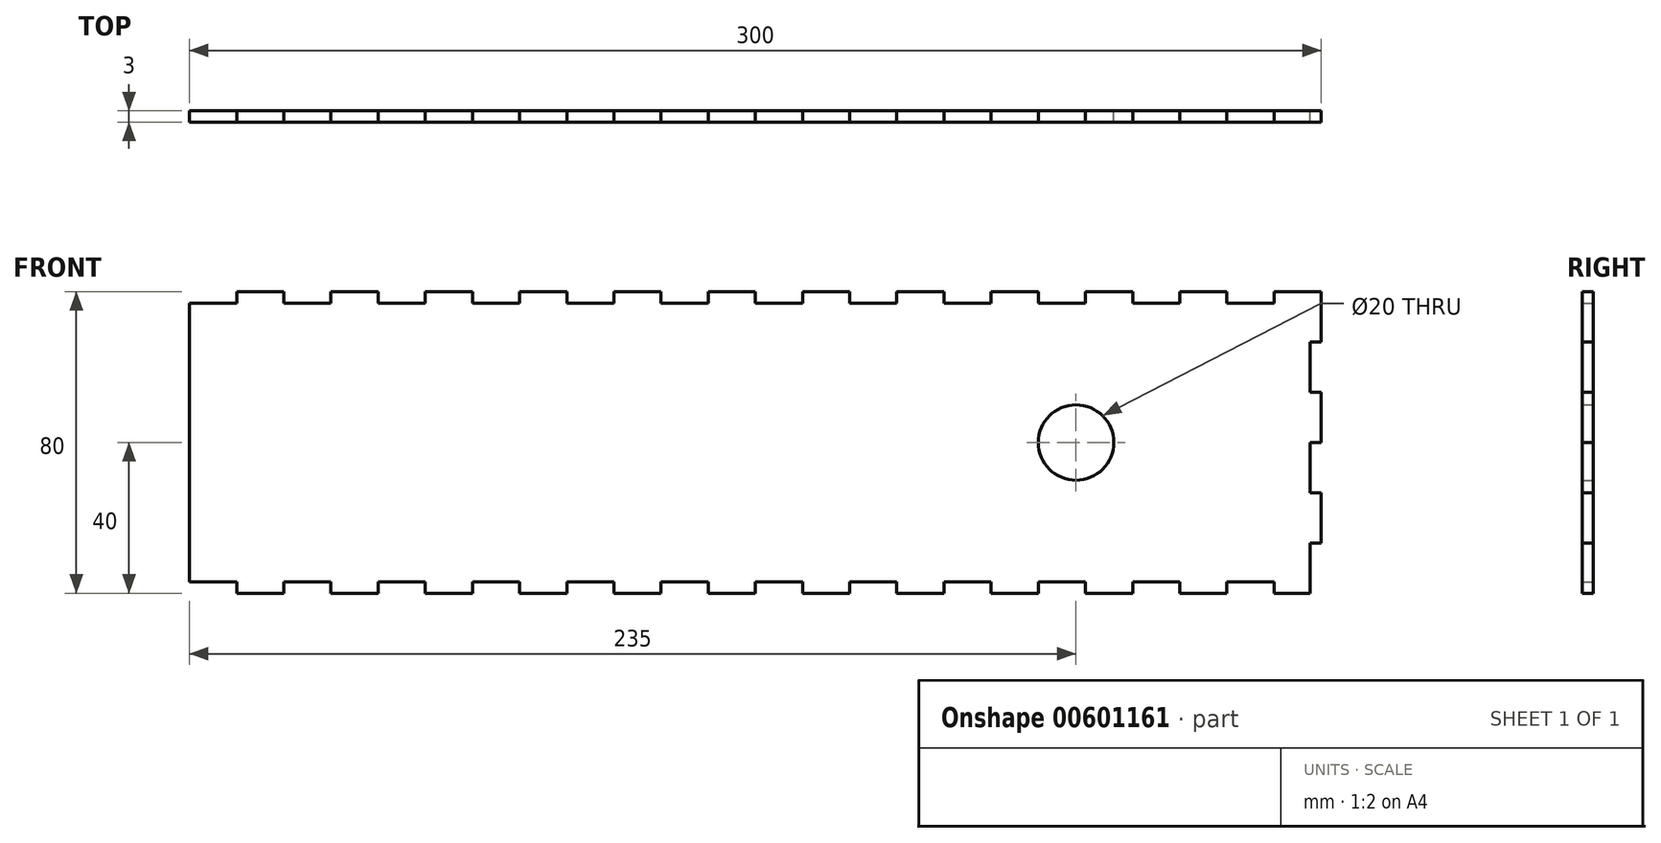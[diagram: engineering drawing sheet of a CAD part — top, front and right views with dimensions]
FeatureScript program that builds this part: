
annotation { "Feature Type Name" : "Feature", "Feature Type Description" : "" }
export const myFeature = defineFeature(function(context is Context, id is Id, definition is map)
    precondition{}
    {
        {
            var Q0;
            Q0=qCreatedBy(makeId("Front.planeOp"),FACE);
            var sketch = newSketch(context, id + "F0", { "sketchPlane" : qUnion([Q0])});
            skLineSegment(sketch, "E0.left", {"start": v(150, -26.67) * mm, "end": v(150, -13.33) * mm});
            skLineSegment(sketch, "E0.right", {"start": v(-150, -37) * mm, "end": v(-150, 37) * mm});
            skPoint(sketch, "E0.middle", {"position": v(0, 0) * mm});
            skLineSegment(sketch, "E1", {"start": v(-137.5, -40) * mm, "end": v(-125, -40) * mm});
            skLineSegment(sketch, "E2", {"start": v(-150, -37) * mm, "end": v(-137.5, -37) * mm});
            skLineSegment(sketch, "E3", {"start": v(-137.5, -37) * mm, "end": v(-137.5, -40) * mm});
            skLineSegment(sketch, "E4", {"start": v(-125, -37) * mm, "end": v(-125, -40) * mm});
            skLineSegment(sketch, "E5", {"start": v(-112.5, -37) * mm, "end": v(-112.5, -40) * mm});
            skLineSegment(sketch, "E6", {"start": v(-100, -37) * mm, "end": v(-100, -40) * mm});
            skLineSegment(sketch, "E7", {"start": v(-75, -37) * mm, "end": v(-75, -40) * mm});
            skLineSegment(sketch, "E8", {"start": v(-62.5, -37) * mm, "end": v(-62.5, -40) * mm});
            skLineSegment(sketch, "E9", {"start": v(-50, -37) * mm, "end": v(-50, -40) * mm});
            skLineSegment(sketch, "E10", {"start": v(-87.5, -37) * mm, "end": v(-87.5, -40) * mm});
            skLineSegment(sketch, "E11", {"start": v(-25, -37) * mm, "end": v(-25, -40) * mm});
            skLineSegment(sketch, "E12", {"start": v(-12.5, -37) * mm, "end": v(-12.5, -40) * mm});
            skLineSegment(sketch, "E13", {"start": v(0, -40) * mm, "end": v(0, -37) * mm});
            skLineSegment(sketch, "E14", {"start": v(-37.5, -37) * mm, "end": v(-37.5, -40) * mm});
            skLineSegment(sketch, "E15.MirrorCS", {"start": v(125, -37) * mm, "end": v(125, -40) * mm});
            skLineSegment(sketch, "E16.MirrorCS", {"start": v(137.5, -37) * mm, "end": v(137.5, -40) * mm});
            skLineSegment(sketch, "E17.MirrorCS", {"start": v(112.5, -37) * mm, "end": v(112.5, -40) * mm});
            skLineSegment(sketch, "E18.MirrorCS", {"start": v(87.5, -37) * mm, "end": v(87.5, -40) * mm});
            skLineSegment(sketch, "E19.MirrorCS", {"start": v(100, -37) * mm, "end": v(100, -40) * mm});
            skLineSegment(sketch, "E20.MirrorCS", {"start": v(75, -37) * mm, "end": v(75, -40) * mm});
            skLineSegment(sketch, "E21.MirrorCS", {"start": v(62.5, -37) * mm, "end": v(62.5, -40) * mm});
            skLineSegment(sketch, "E22.MirrorCS", {"start": v(50, -37) * mm, "end": v(50, -40) * mm});
            skLineSegment(sketch, "E23.MirrorCS", {"start": v(12.5, -37) * mm, "end": v(12.5, -40) * mm});
            skLineSegment(sketch, "E24.MirrorCS", {"start": v(25, -37) * mm, "end": v(25, -40) * mm});
            skLineSegment(sketch, "E25.MirrorCS", {"start": v(37.5, -37) * mm, "end": v(37.5, -40) * mm});
            skPoint(sketch, "E26.orphan", {"position": v(-150, -40) * mm});
            skLineSegment(sketch, "E27.trimOffspring", {"start": v(-125, -37) * mm, "end": v(-112.5, -37) * mm});
            skLineSegment(sketch, "E28.trimOffspring", {"start": v(-112.5, -40) * mm, "end": v(-100, -40) * mm});
            skLineSegment(sketch, "E29.trimOffspring", {"start": v(-100, -37) * mm, "end": v(-87.5, -37) * mm});
            skLineSegment(sketch, "E30.trimOffspring", {"start": v(-87.5, -40) * mm, "end": v(-75, -40) * mm});
            skLineSegment(sketch, "E31.trimOffspring", {"start": v(-75, -37) * mm, "end": v(-62.5, -37) * mm});
            skLineSegment(sketch, "E32.trimOffspring", {"start": v(-62.5, -40) * mm, "end": v(-50, -40) * mm});
            skLineSegment(sketch, "E33.trimOffspring", {"start": v(-50, -37) * mm, "end": v(-37.5, -37) * mm});
            skLineSegment(sketch, "E34.trimOffspring", {"start": v(-37.5, -40) * mm, "end": v(-25, -40) * mm});
            skLineSegment(sketch, "E35.trimOffspring", {"start": v(-25, -37) * mm, "end": v(-12.5, -37) * mm});
            skLineSegment(sketch, "E36.trimOffspring", {"start": v(-12.5, -40) * mm, "end": v(0, -40) * mm});
            skLineSegment(sketch, "E37.trimOffspring", {"start": v(0, -37) * mm, "end": v(12.5, -37) * mm});
            skLineSegment(sketch, "E38.trimOffspring", {"start": v(12.5, -40) * mm, "end": v(25, -40) * mm});
            skLineSegment(sketch, "E39.trimOffspring", {"start": v(25, -37) * mm, "end": v(37.5, -37) * mm});
            skLineSegment(sketch, "E40.trimOffspring", {"start": v(37.5, -40) * mm, "end": v(50, -40) * mm});
            skLineSegment(sketch, "E41.trimOffspring", {"start": v(50, -37) * mm, "end": v(62.5, -37) * mm});
            skLineSegment(sketch, "E42.trimOffspring", {"start": v(62.5, -40) * mm, "end": v(75, -40) * mm});
            skLineSegment(sketch, "E43.trimOffspring", {"start": v(75, -37) * mm, "end": v(87.5, -37) * mm});
            skLineSegment(sketch, "E44.trimOffspring", {"start": v(87.5, -40) * mm, "end": v(100, -40) * mm});
            skLineSegment(sketch, "E45.trimOffspring", {"start": v(100, -37) * mm, "end": v(112.5, -37) * mm});
            skLineSegment(sketch, "E46.trimOffspring", {"start": v(112.5, -40) * mm, "end": v(125, -40) * mm});
            skLineSegment(sketch, "E47.trimOffspring", {"start": v(125, -37) * mm, "end": v(137.5, -37) * mm});
            skLineSegment(sketch, "E48.trimOffspring", {"start": v(137.5, -40) * mm, "end": v(147, -40) * mm});
            skLineSegment(sketch, "E49.MirrorCS", {"start": v(0, 40) * mm, "end": v(0, 37) * mm});
            skLineSegment(sketch, "E50.MirrorCS", {"start": v(-12.5, 37) * mm, "end": v(-12.5, 40) * mm});
            skLineSegment(sketch, "E51.MirrorCS", {"start": v(100, 37) * mm, "end": v(100, 40) * mm});
            skLineSegment(sketch, "E52.MirrorCS", {"start": v(87.5, 37) * mm, "end": v(87.5, 40) * mm});
            skLineSegment(sketch, "E53.MirrorCS", {"start": v(125, 37) * mm, "end": v(125, 40) * mm});
            skLineSegment(sketch, "E54.MirrorCS", {"start": v(-87.5, 37) * mm, "end": v(-87.5, 40) * mm});
            skLineSegment(sketch, "E55.MirrorCS", {"start": v(50, 37) * mm, "end": v(50, 40) * mm});
            skLineSegment(sketch, "E56.MirrorCS", {"start": v(37.5, 37) * mm, "end": v(37.5, 40) * mm});
            skLineSegment(sketch, "E57.MirrorCS", {"start": v(-25, 37) * mm, "end": v(-25, 40) * mm});
            skLineSegment(sketch, "E58.MirrorCS", {"start": v(-50, 37) * mm, "end": v(-50, 40) * mm});
            skLineSegment(sketch, "E59.MirrorCS", {"start": v(-62.5, 37) * mm, "end": v(-62.5, 40) * mm});
            skLineSegment(sketch, "E60.MirrorCS", {"start": v(-112.5, 37) * mm, "end": v(-112.5, 40) * mm});
            skLineSegment(sketch, "E61.MirrorCS", {"start": v(-75, 37) * mm, "end": v(-75, 40) * mm});
            skLineSegment(sketch, "E62.MirrorCS", {"start": v(-100, 37) * mm, "end": v(-100, 40) * mm});
            skLineSegment(sketch, "E63.MirrorCS", {"start": v(112.5, 37) * mm, "end": v(112.5, 40) * mm});
            skLineSegment(sketch, "E64.MirrorCS", {"start": v(12.5, 37) * mm, "end": v(12.5, 40) * mm});
            skLineSegment(sketch, "E65.MirrorCS", {"start": v(75, 37) * mm, "end": v(75, 40) * mm});
            skLineSegment(sketch, "E66.MirrorCS", {"start": v(137.5, 37) * mm, "end": v(137.5, 40) * mm});
            skLineSegment(sketch, "E67.MirrorCS", {"start": v(-125, 37) * mm, "end": v(-125, 40) * mm});
            skLineSegment(sketch, "E68.MirrorCS", {"start": v(-137.5, 37) * mm, "end": v(-137.5, 40) * mm});
            skLineSegment(sketch, "E69.MirrorCS", {"start": v(-37.5, 37) * mm, "end": v(-37.5, 40) * mm});
            skLineSegment(sketch, "E70.MirrorCS", {"start": v(25, 37) * mm, "end": v(25, 40) * mm});
            skLineSegment(sketch, "E71.MirrorCS", {"start": v(62.5, 37) * mm, "end": v(62.5, 40) * mm});
            skLineSegment(sketch, "E72.MirrorCS", {"start": v(-112.5, 40) * mm, "end": v(-100, 40) * mm});
            skLineSegment(sketch, "E73.MirrorCS", {"start": v(87.5, 40) * mm, "end": v(100, 40) * mm});
            skLineSegment(sketch, "E74.MirrorCS", {"start": v(-25, 37) * mm, "end": v(-12.5, 37) * mm});
            skPoint(sketch, "E75.MirrorP", {"position": v(-150, 40) * mm});
            skLineSegment(sketch, "E76.MirrorCS", {"start": v(50, 37) * mm, "end": v(62.5, 37) * mm});
            skLineSegment(sketch, "E77.MirrorCS", {"start": v(12.5, 40) * mm, "end": v(25, 40) * mm});
            skLineSegment(sketch, "E78.MirrorCS", {"start": v(62.5, 40) * mm, "end": v(75, 40) * mm});
            skLineSegment(sketch, "E79.MirrorCS", {"start": v(125, 37) * mm, "end": v(137.5, 37) * mm});
            skLineSegment(sketch, "E80.MirrorCS", {"start": v(-75, 37) * mm, "end": v(-62.5, 37) * mm});
            skLineSegment(sketch, "E81.MirrorCS", {"start": v(0, 37) * mm, "end": v(12.5, 37) * mm});
            skLineSegment(sketch, "E82.MirrorCS", {"start": v(-150, 37) * mm, "end": v(-150, -40) * mm});
            skLineSegment(sketch, "E83.MirrorCS", {"start": v(-87.5, 40) * mm, "end": v(-75, 40) * mm});
            skLineSegment(sketch, "E84.MirrorCS", {"start": v(-50, 37) * mm, "end": v(-37.5, 37) * mm});
            skLineSegment(sketch, "E85.MirrorCS", {"start": v(75, 37) * mm, "end": v(87.5, 37) * mm});
            skLineSegment(sketch, "E86.MirrorCS", {"start": v(-125, 37) * mm, "end": v(-112.5, 37) * mm});
            skLineSegment(sketch, "E87.MirrorCS", {"start": v(25, 37) * mm, "end": v(37.5, 37) * mm});
            skLineSegment(sketch, "E88.MirrorCS", {"start": v(100, 37) * mm, "end": v(112.5, 37) * mm});
            skLineSegment(sketch, "E89.MirrorCS", {"start": v(-12.5, 40) * mm, "end": v(0, 40) * mm});
            skLineSegment(sketch, "E90.MirrorCS", {"start": v(-100, 37) * mm, "end": v(-87.5, 37) * mm});
            skLineSegment(sketch, "E91.MirrorCS", {"start": v(-150, 37) * mm, "end": v(-137.5, 37) * mm});
            skLineSegment(sketch, "E92.MirrorCS", {"start": v(-137.5, 40) * mm, "end": v(-125, 40) * mm});
            skLineSegment(sketch, "E93.MirrorCS", {"start": v(137.5, 40) * mm, "end": v(150, 40) * mm});
            skLineSegment(sketch, "E94.MirrorCS", {"start": v(-62.5, 40) * mm, "end": v(-50, 40) * mm});
            skLineSegment(sketch, "E95.MirrorCS", {"start": v(150, 40) * mm, "end": v(150, 26.67) * mm});
            skLineSegment(sketch, "E96.MirrorCS", {"start": v(112.5, 40) * mm, "end": v(125, 40) * mm});
            skLineSegment(sketch, "E97.MirrorCS", {"start": v(-37.5, 40) * mm, "end": v(-25, 40) * mm});
            skLineSegment(sketch, "E98.MirrorCS", {"start": v(37.5, 40) * mm, "end": v(50, 40) * mm});
            skPoint(sketch, "E99.MirrorCS.end.orphan", {"position": v(-125, 40) * mm});
            skPoint(sketch, "E99.MirrorCS.start.orphan", {"position": v(-137.5, 40) * mm});
            skCircle(sketch, "E100", {"center": v(85, 0) * mm, "radius": 10 * mm});
            skLineSegment(sketch, "E101", {"start": v(147, 26.67) * mm, "end": v(147, 13.33) * mm});
            skLineSegment(sketch, "E102", {"start": v(147, 26.67) * mm, "end": v(150, 26.67) * mm});
            skLineSegment(sketch, "E103", {"start": v(147, 13.33) * mm, "end": v(150, 13.33) * mm});
            skLineSegment(sketch, "E104", {"start": v(147, 0) * mm, "end": v(150, 0) * mm});
            skLineSegment(sketch, "E105", {"start": v(147, -13.33) * mm, "end": v(150, -13.33) * mm});
            skLineSegment(sketch, "E106", {"start": v(147, -26.67) * mm, "end": v(150, -26.67) * mm});
            skLineSegment(sketch, "E107.trimOffspring", {"start": v(150, 13.33) * mm, "end": v(150, 0) * mm});
            skLineSegment(sketch, "E108.trimOffspring", {"start": v(150, 26.67) * mm, "end": v(150, 40) * mm});
            skLineSegment(sketch, "E109.trimOffspring", {"start": v(147, 0) * mm, "end": v(147, -13.33) * mm});
            skLineSegment(sketch, "E110.trimOffspring", {"start": v(150, 0) * mm, "end": v(150, 13.33) * mm});
            skLineSegment(sketch, "E111.trimOffspring", {"start": v(150, -13.33) * mm, "end": v(150, -26.67) * mm});
            skLineSegment(sketch, "E112.trimOffspring", {"start": v(147, -26.67) * mm, "end": v(147, -40) * mm});
            skPoint(sketch, "E113.orphan", {"position": v(150, -40) * mm});
            skSolve(sketch);
        }
        {
            var Q0;
            Q0=makeQuery(id+"F0.imprint","IMPRINT",FACE,{"disambiguationData":[TD([[makeQuery(id+"F0.imprint","IMPRINT",EDGE,{"derivedFrom":sQuery(id+"F0.wireOp",EDGE,"E1")}),1.0]])]});
            extrude(context, id + "F1", {"entities" : qUnion([Q0]), "depth" : 3 * mm, "offsetDistance" : 25 * mm});
        }
    });
